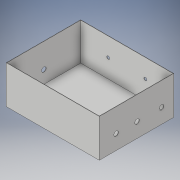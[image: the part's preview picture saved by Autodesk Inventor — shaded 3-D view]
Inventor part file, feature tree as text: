
AUTODESK INVENTOR PART (.ipt)
format: ipt  version: 2018 (Build 220112000, 112)  size: 142,848 bytes
history: native  units: in
note: dims shown in document units (in); Inventor stores cm internally (conversion verified against a paired STEP export)
features: extrude x5, sketch x5
ambient origin geometry x8: Origin, YZ Plane, XZ Plane, XY Plane, X Axis, Y Axis, Z Axis, Center Point
bodies: Solid1 (feature_tree)
feature tree (10):
  extrude  "Extrusion1"  Depth=4.0in
  extrude  "Extrusion2"  Depth=4.96in
  extrude  "Extrusion3"  Depth=2.0in TaperAngle=0.0deg
  extrude  "Extrusion4"  Depth=0.164in
  extrude  "Extrusion5"  Depth=0.25in
  sketch  "Sketch1"  dims[d0=5.0in d1=4.0in]
  sketch  "Sketch2"  dims[d2=0.04in d3=0.0in d4=4.96in]
  sketch  "Sketch3"  dims[d5=3.96in d6=2.0in d7=0.0in]
  sketch  "Sketch4"  dims[d10=0.164in d12=0.164in]
  sketch  "Sketch5"  dims[d13=0.0in d14=0.0in d15=0.25in d16=0.0in d17=0.0in d18=0.0115in d19=0.0in d20=0.625in d21=1.313in d22=180.0deg d23=1.125in d24=0.0in d25=1.125in d26=0.25in d27=0.25in d28=0.25in d29=0.0in d30=0.0in]
